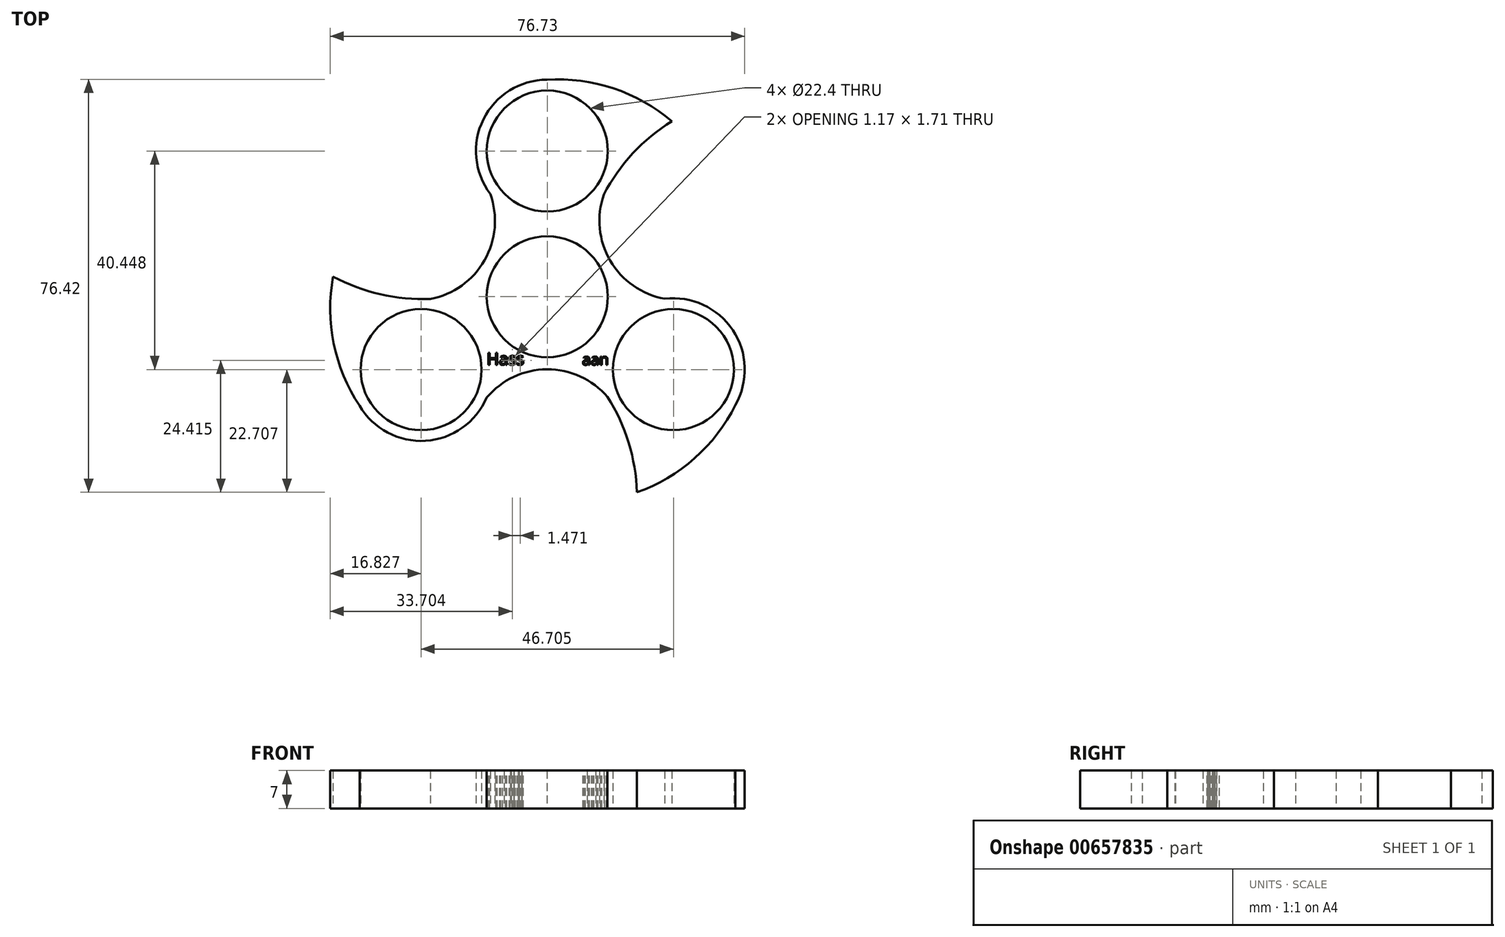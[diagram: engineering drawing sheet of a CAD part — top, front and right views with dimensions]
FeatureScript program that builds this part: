
annotation { "Feature Type Name" : "Feature", "Feature Type Description" : "" }
export const myFeature = defineFeature(function(context is Context, id is Id, definition is map)
    precondition{}
    {
        {
            var Q0;
            Q0=qCreatedBy(makeId("Top.planeOp"),FACE);
            var sketch = newSketch(context, id + "F0", { "sketchPlane" : qUnion([Q0])});
            skCircle(sketch, "E0", {"center": v(0, 0) * mm, "radius": 11.2 * mm});
            skArc(sketch, "E1", {"start": v(10.47, 18.92) * mm, "mid": v(11.4, 20.3) * mm, "end": v(12.14, 21.78) * mm});
            skCircle(sketch, "E2", {"center": v(0, 26.97) * mm, "radius": 11.2 * mm});
            skArc(sketch, "E3.1.0", {"start": v(-21.62, -0.4) * mm, "mid": v(-23.28, -0.28) * mm, "end": v(-24.93, -0.38) * mm});
            skCircle(sketch, "E3.1.1", {"center": v(-23.35, -13.48) * mm, "radius": 11.2 * mm});
            skArc(sketch, "E3.2.0", {"start": v(11.15, -18.52) * mm, "mid": v(11.88, -20.02) * mm, "end": v(12.8, -21.4) * mm});
            skCircle(sketch, "E3.2.1", {"center": v(23.35, -13.48) * mm, "radius": 11.2 * mm});
            skArc(sketch, "E4", {"start": v(10.47, 18.92) * mm, "mid": v(11.66, 6.67) * mm, "end": v(21.76, -0.38) * mm});
            skArc(sketch, "E5.1.0", {"start": v(-21.62, -0.4) * mm, "mid": v(-11.6, 6.77) * mm, "end": v(-10.55, 19.03) * mm});
            skArc(sketch, "E5.2.0", {"start": v(11.15, -18.52) * mm, "mid": v(-0.06, -13.43) * mm, "end": v(-11.2, -18.66) * mm});
            skArc(sketch, "E6", {"start": v(23.05, 32.47) * mm, "mid": v(12.24, 38.57) * mm, "end": v(-0.07, 40.17) * mm});
            skPoint(sketch, "E6.endSnap0", {"position": v(0.07, 40.17) * mm});
            skArc(sketch, "E7", {"start": v(23.05, 32.47) * mm, "mid": v(15.85, 26.54) * mm, "end": v(10.47, 18.92) * mm});
            skArc(sketch, "E8.1.0", {"start": v(-39.64, 3.72) * mm, "mid": v(-39.52, -8.69) * mm, "end": v(-34.75, -20.14) * mm});
            skArc(sketch, "E8.1.1", {"start": v(-39.64, 3.72) * mm, "mid": v(-30.9, 0.46) * mm, "end": v(-21.62, -0.4) * mm});
            skArc(sketch, "E8.2.0", {"start": v(16.6, -36.2) * mm, "mid": v(27.28, -29.88) * mm, "end": v(34.82, -20.02) * mm});
            skArc(sketch, "E8.2.1", {"start": v(16.6, -36.2) * mm, "mid": v(15.06, -27) * mm, "end": v(11.15, -18.52) * mm});
            skArc(sketch, "E9.trimOffspring", {"start": v(0.07, 40.17) * mm, "mid": v(-11.8, 32.9) * mm, "end": v(-10.55, 19.03) * mm});
            skArc(sketch, "E10.trimOffspring", {"start": v(-34.75, -20.14) * mm, "mid": v(-22.52, -26.66) * mm, "end": v(-11.2, -18.66) * mm});
            skArc(sketch, "E11.trimOffspring", {"start": v(34.82, -20.02) * mm, "mid": v(34.34, -6.17) * mm, "end": v(21.76, -0.38) * mm});
            skSolve(sketch);
        }
        {
            var Q0;
            Q0=makeQuery(id+"F0.imprint","IMPRINT",FACE,{"disambiguationData":[TD([[makeQuery(id+"F0.imprint","IMPRINT",EDGE,{"derivedFrom":sQuery(id+"F0.wireOp",EDGE,"E0")}),-1.0]])]});
            extrude(context, id + "F1", {"entities" : qUnion([Q0]), "depth" : 7 * mm, "offsetDistance" : 25 * mm});
        }
        {
            var Q0;
            Q0=makeQuery(id+"F1.opExtrude","CAP_FACE",FACE,{"disambiguationData":[OSD([sQuery(id+"F0.wireOp",EDGE,"E0"),sQuery(id+"F0.wireOp",EDGE,"E1"),sQuery(id+"F0.wireOp",EDGE,"E2"),sQuery(id+"F0.wireOp",EDGE,"E3.1.0"),sQuery(id+"F0.wireOp",EDGE,"E3.1.1"),sQuery(id+"F0.wireOp",EDGE,"E3.2.0"),sQuery(id+"F0.wireOp",EDGE,"E3.2.1"),sQuery(id+"F0.wireOp",EDGE,"E4"),sQuery(id+"F0.wireOp",EDGE,"E5.1.0"),sQuery(id+"F0.wireOp",EDGE,"E5.2.0")])],"isStart":false});
            var sketch = newSketch(context, id + "F2", { "sketchPlane" : qUnion([Q0])});
            skText(sketch, "E12", { "text": "Hass", "fontName": "OpenSans-Regular.ttf"});
            const initialGuessF2  = {"E12": [-0.01121, -0.0126, 1, 0, 0.00222]};
            skSetInitialGuess(sketch, initialGuessF2);
            skSolve(sketch);
        }
        {
            var Q0;
            Q0=qSketchRegion(id+"F2",true);
            extrude(context, id + "F3", {"entities" : qUnion([Q0]), "operationType" : NewBodyOperationType.REMOVE, "oppositeDirection" : true, "depth" : 13.4 * mm, "offsetDistance" : 25 * mm});
        }
        {
            var Q0;
            {var subQ0=sQuery(id+"F0.wireOp",EDGE,"E5.1.0");var subQ1=sQuery(id+"F0.wireOp",EDGE,"E4");var subQ2=sQuery(id+"F0.wireOp",EDGE,"E3.2.1");var subQ3=sQuery(id+"F0.wireOp",EDGE,"E3.2.0");var subQ4=sQuery(id+"F0.wireOp",EDGE,"E3.1.1");var subQ5=sQuery(id+"F0.wireOp",EDGE,"E5.2.0");var subQ6=sQuery(id+"F0.wireOp",EDGE,"E0");var subQ7=sQuery(id+"F0.wireOp",EDGE,"E3.1.0");var subQ8=sQuery(id+"F0.wireOp",EDGE,"E1");var subQ9=sQuery(id+"F0.wireOp",EDGE,"E2");Q0=makeQuery(id+"F3.boolean.opBoolean","SPLIT",FACE,{"disambiguationData":[TD([makeQuery(id+"F1.opExtrude","SWEPT_FACE",FACE,{"disambiguationData":[OSD([subQ6])]})])],"derivedFrom":makeQuery(id+"F1.opExtrude","CAP_FACE",FACE,{"disambiguationData":[OSD([subQ6,subQ8,subQ9,subQ7,subQ4,subQ3,subQ2,subQ1,subQ0,subQ5])],"isStart":false})});}
            var sketch = newSketch(context, id + "F4", { "sketchPlane" : qUnion([Q0])});
            skText(sketch, "E13", { "text": "aan", "fontName": "OpenSans-Regular.ttf"});
            const initialGuessF4  = {"E13": [0.00646, -0.01262, 1, 0, 0.00205]};
            skSetInitialGuess(sketch, initialGuessF4);
            skSolve(sketch);
        }
        {
            var Q0;
            Q0=qSketchRegion(id+"F4",true);
            extrude(context, id + "F5", {"entities" : qUnion([Q0]), "operationType" : NewBodyOperationType.REMOVE, "oppositeDirection" : true, "depth" : 9.9 * mm, "offsetDistance" : 25 * mm});
        }
    });
